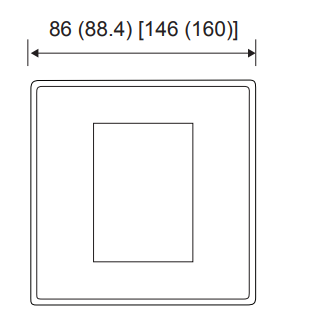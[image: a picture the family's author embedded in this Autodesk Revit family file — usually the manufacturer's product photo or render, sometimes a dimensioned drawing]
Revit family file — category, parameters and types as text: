
# Revit family: Fascia Panel_230S
name_source: partatom
category: Electrical Fixtures
revit_build: Autodesk Revit 2018 (Build: 20170223_1515(x64)
units: mm (PartAtom-declared; Revit-internal decimal feet)

## family parameters
Always vertical = Yes
Cut with Voids When Loaded = No
Maintain Annotation Orientation = No
Part Type = Normal
Room Calculation Point = No
Round Connector Dimension = Use Diameter
Shared = No
Work Plane-Based = Yes

## types (1)
- SG white plastic plate with grid
    Default Elevation = 0 mm  [stored 0 ft]
    Manufacturer = Helvar
    Model = 230 S
    Single chassis dimension = 86 mm × 86 mm × 5.9 mm
    Single frame dimension = 88.4 mm × 88.4 mm × 4.5 mm
(Plastic: 88.4 mm × 88.4 mm × 4.5
mm)
    Single frame kit -net weight = 100 g
    Single frame kit-shipping weight = 130g

note: [stored X ft] marks values corroborated as IEEE doubles in the binary element streams (Revit-internal decimal feet)

## geometry (parser evidence)
native form markers: Sweep x5
no freeform markers — native parametric forms only
